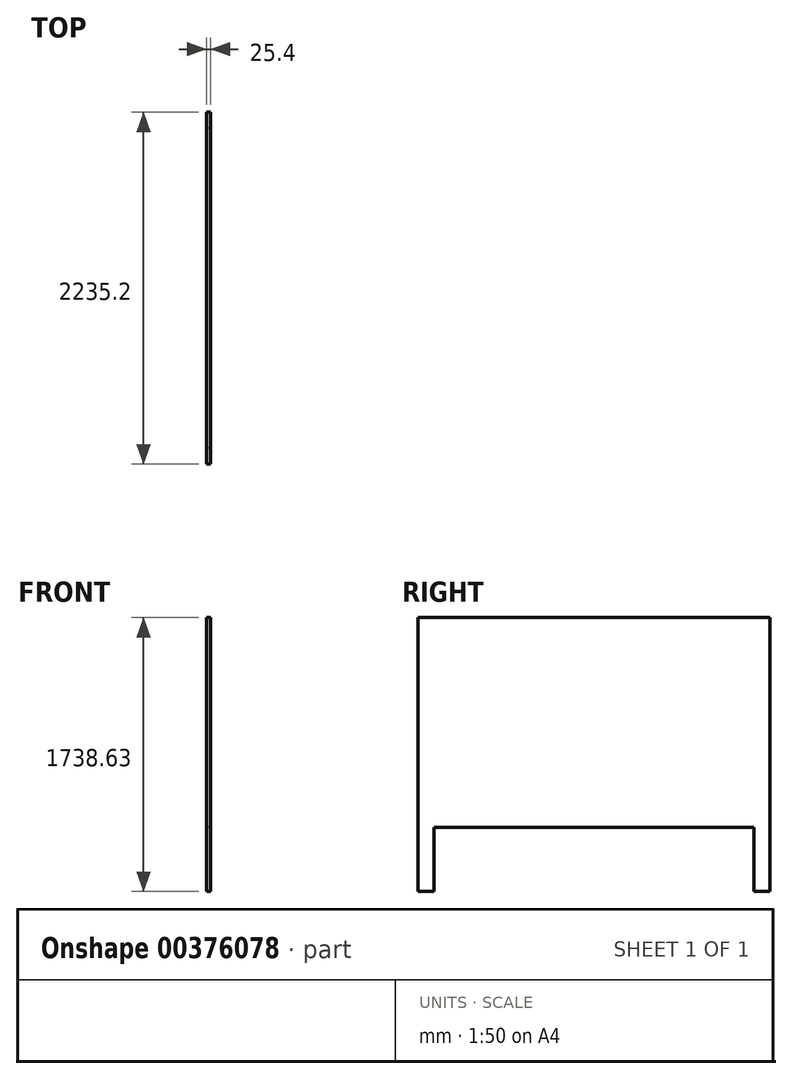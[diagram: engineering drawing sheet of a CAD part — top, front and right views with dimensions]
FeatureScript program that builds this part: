
annotation { "Feature Type Name" : "Feature", "Feature Type Description" : "" }
export const myFeature = defineFeature(function(context is Context, id is Id, definition is map)
    precondition{}
    {
        {
            var Q0;
            Q0=qCreatedBy(makeId("Right.planeOp"),FACE);
            var sketch = newSketch(context, id + "F0", { "sketchPlane" : qUnion([Q0])});
            skLineSegment(sketch, "E0", {"start": v(-1344.55, 373.25) * mm, "end": v(890.65, 373.25) * mm});
            skLineSegment(sketch, "E1", {"start": v(-1344.55, 220.85) * mm, "end": v(890.65, 220.85) * mm});
            skLineSegment(sketch, "E2", {"start": v(890.65, 220.85) * mm, "end": v(890.65, 373.25) * mm});
            skLineSegment(sketch, "E3", {"start": v(-1344.55, 220.85) * mm, "end": v(-1344.55, 373.25) * mm});
            skLineSegment(sketch, "E4", {"start": v(890.65, 220.85) * mm, "end": v(890.65, -185.55) * mm});
            skLineSegment(sketch, "E5", {"start": v(890.65, -185.55) * mm, "end": v(789.05, -185.55) * mm});
            skLineSegment(sketch, "E6", {"start": v(789.05, -185.55) * mm, "end": v(789.05, 220.85) * mm});
            skLineSegment(sketch, "E7", {"start": v(-1344.55, 220.85) * mm, "end": v(-1344.55, -185.55) * mm});
            skLineSegment(sketch, "E8", {"start": v(-1344.55, -185.55) * mm, "end": v(-1242.95, -185.55) * mm});
            skLineSegment(sketch, "E9", {"start": v(-1242.95, -185.55) * mm, "end": v(-1242.95, 220.85) * mm});
            skLineSegment(sketch, "E10", {"start": v(-1344.55, 373.25) * mm, "end": v(-1344.55, 1553.08) * mm});
            skLineSegment(sketch, "E11", {"start": v(-1344.55, 1553.08) * mm, "end": v(890.65, 1553.08) * mm});
            skLineSegment(sketch, "E12", {"start": v(890.65, 1553.08) * mm, "end": v(890.65, 373.25) * mm});
            skPoint(sketch, "E13", {"position": v(-1723, -185.55) * mm});
            skPoint(sketch, "E14", {"position": v(890.65, -185.55) * mm});
            skPoint(sketch, "E15", {"position": v(1043.81, -185.55) * mm});
            skPoint(sketch, "E16", {"position": v(1043.81, 576.45) * mm});
            skPoint(sketch, "E17", {"position": v(-1723, 1973.45) * mm});
            skLineSegment(sketch, "E18", {"start": v(-1723, 1973.45) * mm, "end": v(-4605.06, 576.45) * mm});
            skLineSegment(sketch, "E19", {"start": v(1043.81, 576.45) * mm, "end": v(3927.32, 1973.45) * mm});
            skLineSegment(sketch, "E20", {"start": v(-2607.15, 1544.89) * mm, "end": v(-2607.15, -185.55) * mm});
            skLineSegment(sketch, "E21", {"start": v(3059.33, 1552.93) * mm, "end": v(3059.33, -185.55) * mm});
            skLineSegment(sketch, "E22", {"start": v(-226.95, 373.25) * mm, "end": v(-226.95, 2100.45) * mm});
            skSolve(sketch);
        }
        {
            var Q0;
            Q0 = qSketchRegion(id + "F0", true);
            extrude(context, id + "F1", {"entities" : qUnion([Q0]), "depth" : 25.4 * mm});
        }
    });
